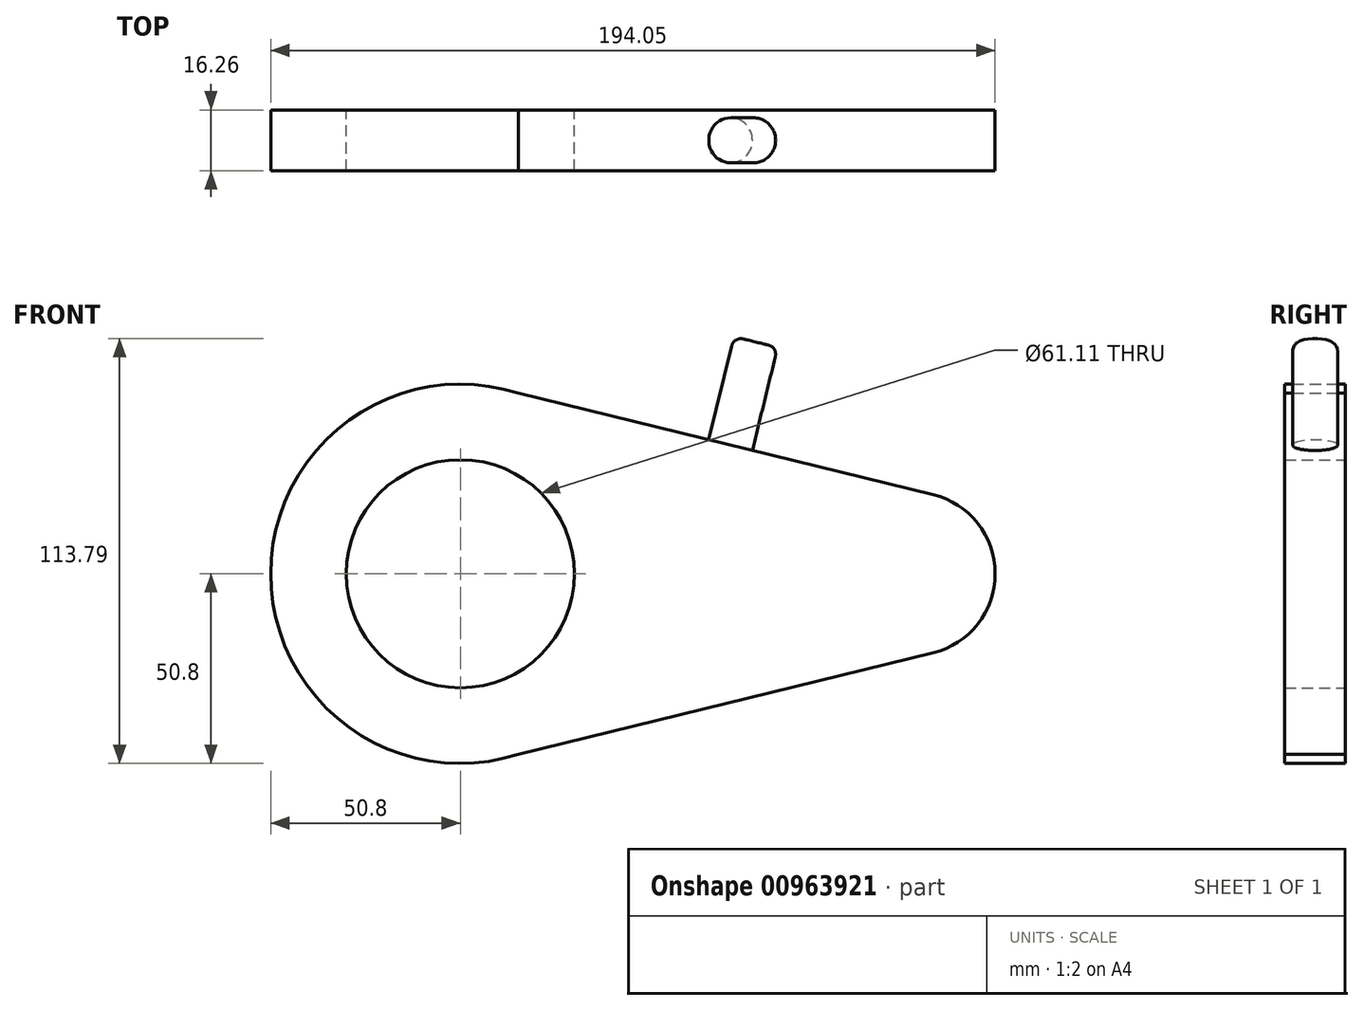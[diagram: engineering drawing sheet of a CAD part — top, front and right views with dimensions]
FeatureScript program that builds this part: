
annotation { "Feature Type Name" : "Feature", "Feature Type Description" : "" }
export const myFeature = defineFeature(function(context is Context, id is Id, definition is map)
    precondition{}
    {
        {
            var Q0;
            Q0=qCreatedBy(makeId("Front.planeOp"),FACE);
            var sketch = newSketch(context, id + "F0", { "sketchPlane" : qUnion([Q0])});
            skCircle(sketch, "E0", {"center": v(0, 0) * mm, "radius": 50.8 * mm});
            skCircle(sketch, "E1", {"center": v(121.43, 0) * mm, "radius": 21.82 * mm});
            skLineSegment(sketch, "E2", {"start": v(15.58, 48.35) * mm, "end": v(126.6, 21.2) * mm});
            skLineSegment(sketch, "E3", {"start": v(15.58, -48.35) * mm, "end": v(126.6, -21.2) * mm});
            skCircle(sketch, "E4", {"center": v(0, 0) * mm, "radius": 30.55 * mm});
            skSolve(sketch);
        }
        {
            var Q0;
            Q0 = qSketchRegion(id + "F0", true);
            extrude(context, id + "F1", {"entities" : qUnion([Q0]), "endBound" : BoundingType.SYMMETRIC, "depth" : 16.26 * mm, "offsetDistance" : 25.4 * mm});
        }
        {
            var Q0;
            Q0=makeQuery(id+"F1.opExtrude","SWEPT_FACE",FACE,{"disambiguationData":[OSD([sQuery(id+"F0.wireOp",EDGE,"E2")])]});
            var sketch = newSketch(context, id + "F2", { "sketchPlane" : qUnion([Q0])});
            skLineSegment(sketch, "E5", {"start": v(117.95, 0) * mm, "end": v(62.13, 0) * mm});
            skCircle(sketch, "E6", {"center": v(62.13, 0) * mm, "radius": 6.02 * mm});
            skSolve(sketch);
        }
        {
            var Q0;
            Q0 = qSketchRegion(id + "F2", true);
            extrude(context, id + "F3", {"entities" : qUnion([Q0]), "operationType" : NewBodyOperationType.ADD, "depth" : 28.45 * mm, "offsetDistance" : 25.4 * mm});
        }
        {
            var Q0;
            Q0=makeQuery(id+"F3.opExtrude","CAP_EDGE",EDGE,{"disambiguationData":[OSD([sQuery(id+"F2.wireOp",EDGE,"E6")])],"isStart":false});
            var Q1;
            Q1=makeQuery(id+"F3.opExtrude","CAP_EDGE",EDGE,{"disambiguationData":[OSD([sQuery(id+"F2.wireOp",EDGE,"E6")])],"isStart":true});
            fillet(context, id + "F4", {"entities" : qUnion([Q0, Q1]), "radius" : 2.54 * mm, "tangentPropagation" : true, "allowEdgeOverflow" : false});
        }
    });
